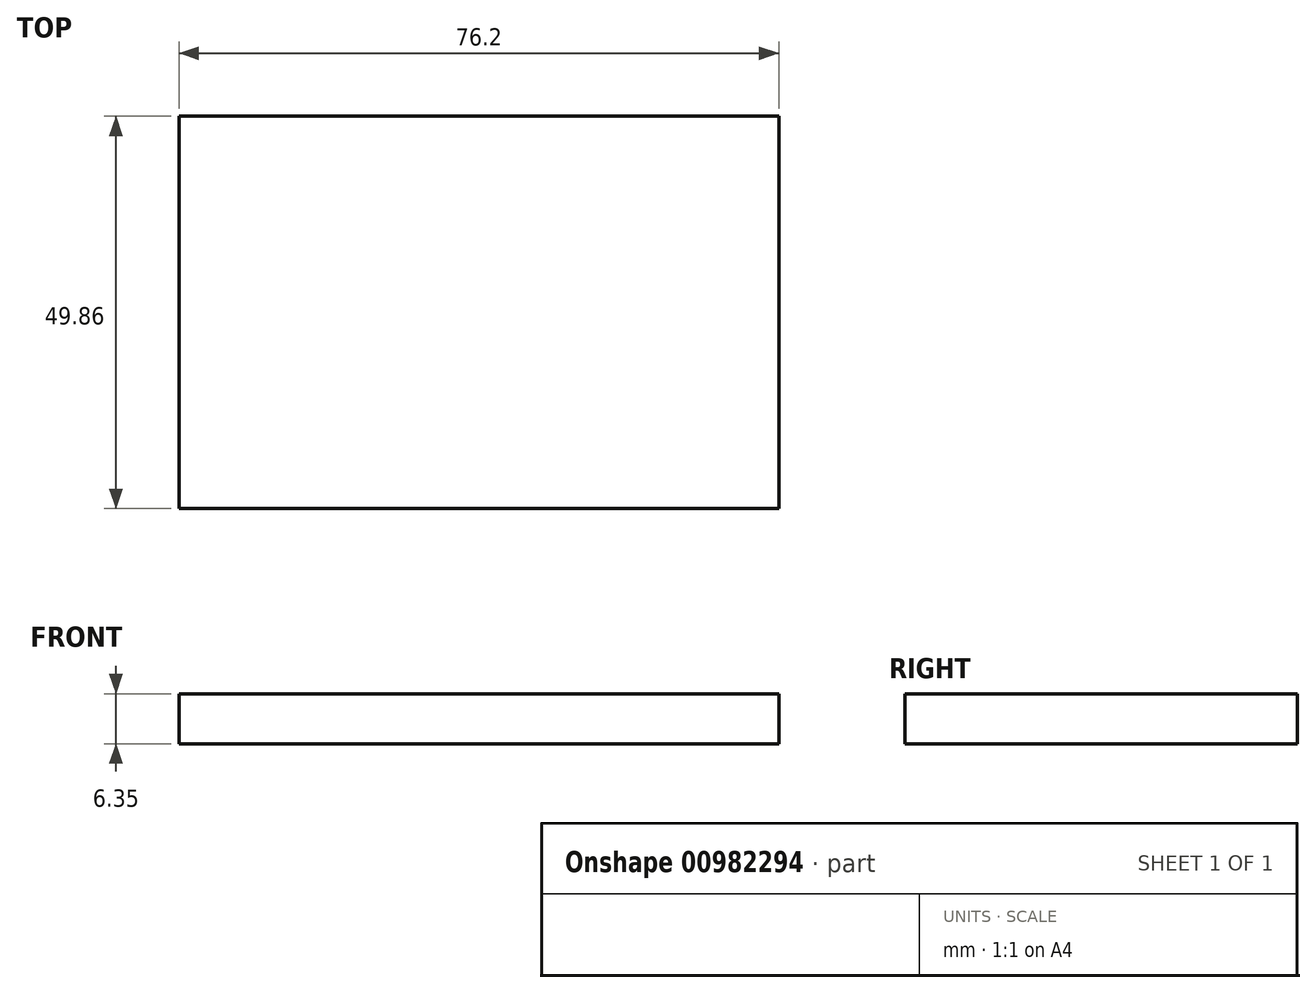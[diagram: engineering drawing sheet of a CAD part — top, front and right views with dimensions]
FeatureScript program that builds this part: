
annotation { "Feature Type Name" : "Feature", "Feature Type Description" : "" }
export const myFeature = defineFeature(function(context is Context, id is Id, definition is map)
    precondition{}
    {
        {
            var Q0;
            Q0=qCreatedBy(makeId("Top.planeOp"),FACE);
            var sketch = newSketch(context, id + "F0", { "sketchPlane" : qUnion([Q0])});
            skLineSegment(sketch, "E0.bottom", {"start": v(-38.1, 24.93) * mm, "end": v(38.1, 24.93) * mm});
            skLineSegment(sketch, "E0.top", {"start": v(-38.1, -24.93) * mm, "end": v(38.1, -24.93) * mm});
            skLineSegment(sketch, "E0.left", {"start": v(-38.1, 24.93) * mm, "end": v(-38.1, -24.93) * mm});
            skLineSegment(sketch, "E0.right", {"start": v(38.1, 24.93) * mm, "end": v(38.1, -24.93) * mm});
            skPoint(sketch, "E0.middle", {"position": v(0, 0) * mm});
            skSolve(sketch);
        }
        {
            var Q0;
            Q0=makeQuery(id+"F0.imprint","IMPRINT",FACE,{"disambiguationData":[TD([[makeQuery(id+"F0.imprint","IMPRINT",EDGE,{"derivedFrom":sQuery(id+"F0.wireOp",EDGE,"E0.bottom")}),-1.0]])]});
            var sketch = newSketch(context, id + "F1", { "sketchPlane" : qUnion([Q0])});
            skSolve(sketch);
        }
        {
            var Q0;
            Q0=makeQuery(id+"F1.imprint","IMPRINT",FACE,{"disambiguationData":[TD([[makeQuery(id+"F1.imprint","IMPRINT",EDGE,{"derivedFrom":makeQuery(id+"F0.imprint","IMPRINT",EDGE,{"derivedFrom":sQuery(id+"F0.wireOp",EDGE,"E0.bottom")})}),-1.0]])]});
            var Q1;
            Q1=makeQuery(id+"F0.imprint","IMPRINT",FACE,{"disambiguationData":[TD([[makeQuery(id+"F0.imprint","IMPRINT",EDGE,{"derivedFrom":sQuery(id+"F0.wireOp",EDGE,"E0.bottom")}),-1.0]])]});
            extrude(context, id + "F2", {"entities" : qUnion([Q0, Q1]), "depth" : 6.35 * mm, "offsetDistance" : 25.4 * mm});
        }
    });
